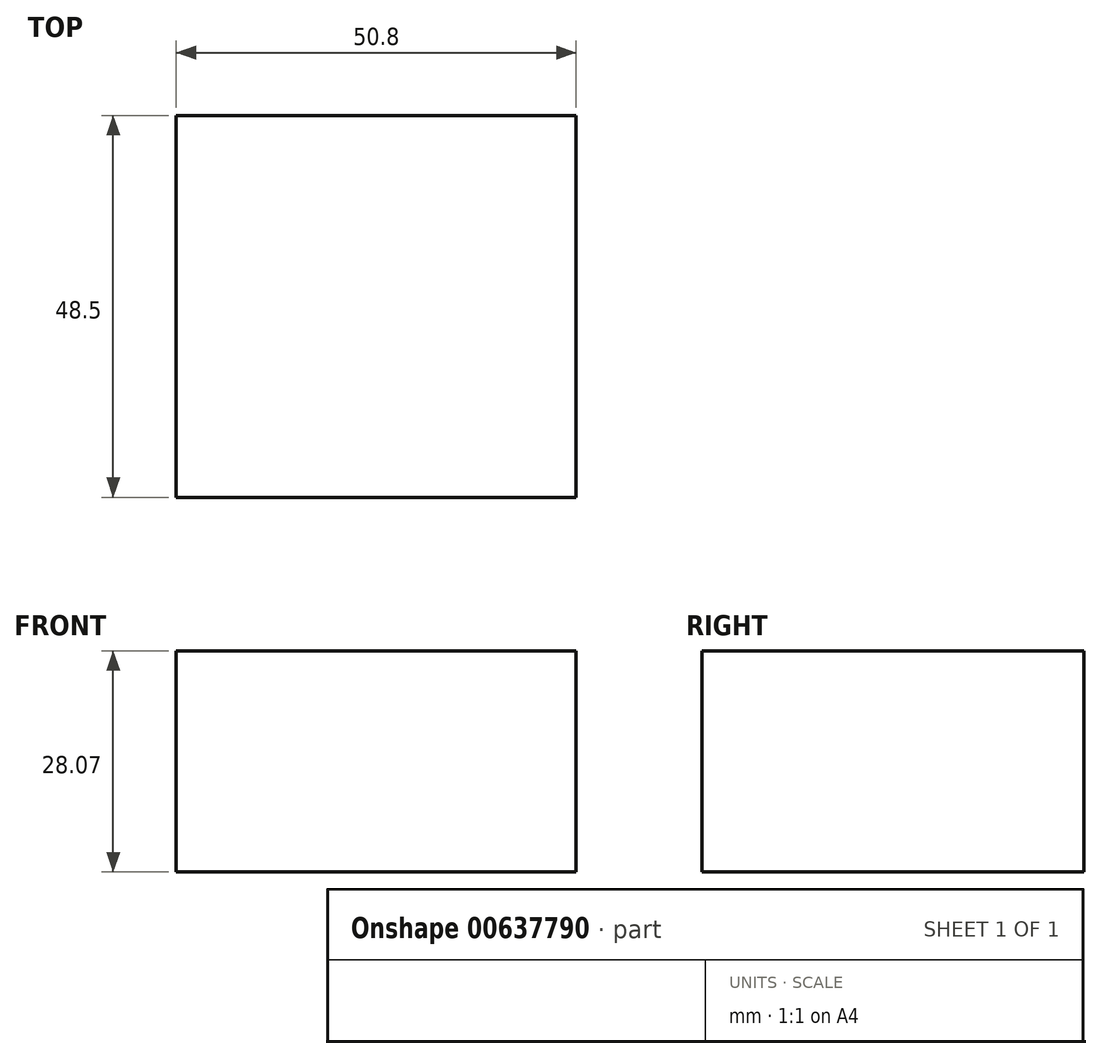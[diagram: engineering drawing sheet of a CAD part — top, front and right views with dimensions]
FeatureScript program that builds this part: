
annotation { "Feature Type Name" : "Feature", "Feature Type Description" : "" }
export const myFeature = defineFeature(function(context is Context, id is Id, definition is map)
    precondition{}
    {
        {
            var Q0;
            Q0=qCreatedBy(makeId("Right.planeOp"),FACE);
            var sketch = newSketch(context, id + "F0", { "sketchPlane" : qUnion([Q0])});
            skLineSegment(sketch, "E0.bottom", {"start": v(61.01, -40.58) * mm, "end": v(12.5, -40.58) * mm});
            skLineSegment(sketch, "E0.top", {"start": v(61.01, -12.5) * mm, "end": v(12.5, -12.5) * mm});
            skLineSegment(sketch, "E0.left", {"start": v(61.01, -40.58) * mm, "end": v(61.01, -12.5) * mm});
            skLineSegment(sketch, "E0.right", {"start": v(12.5, -40.58) * mm, "end": v(12.5, -12.5) * mm});
            skSolve(sketch);
        }
        {
            var Q0;
            Q0=makeQuery(id+"F0.imprint","IMPRINT",FACE,{"disambiguationData":[TD([[makeQuery(id+"F0.imprint","IMPRINT",EDGE,{"derivedFrom":sQuery(id+"F0.wireOp",EDGE,"E0.bottom")}),-1.0]])]});
            extrude(context, id + "F1", {"entities" : qUnion([Q0]), "depth" : 50.8 * mm, "offsetDistance" : 25.4 * mm});
        }
    });
